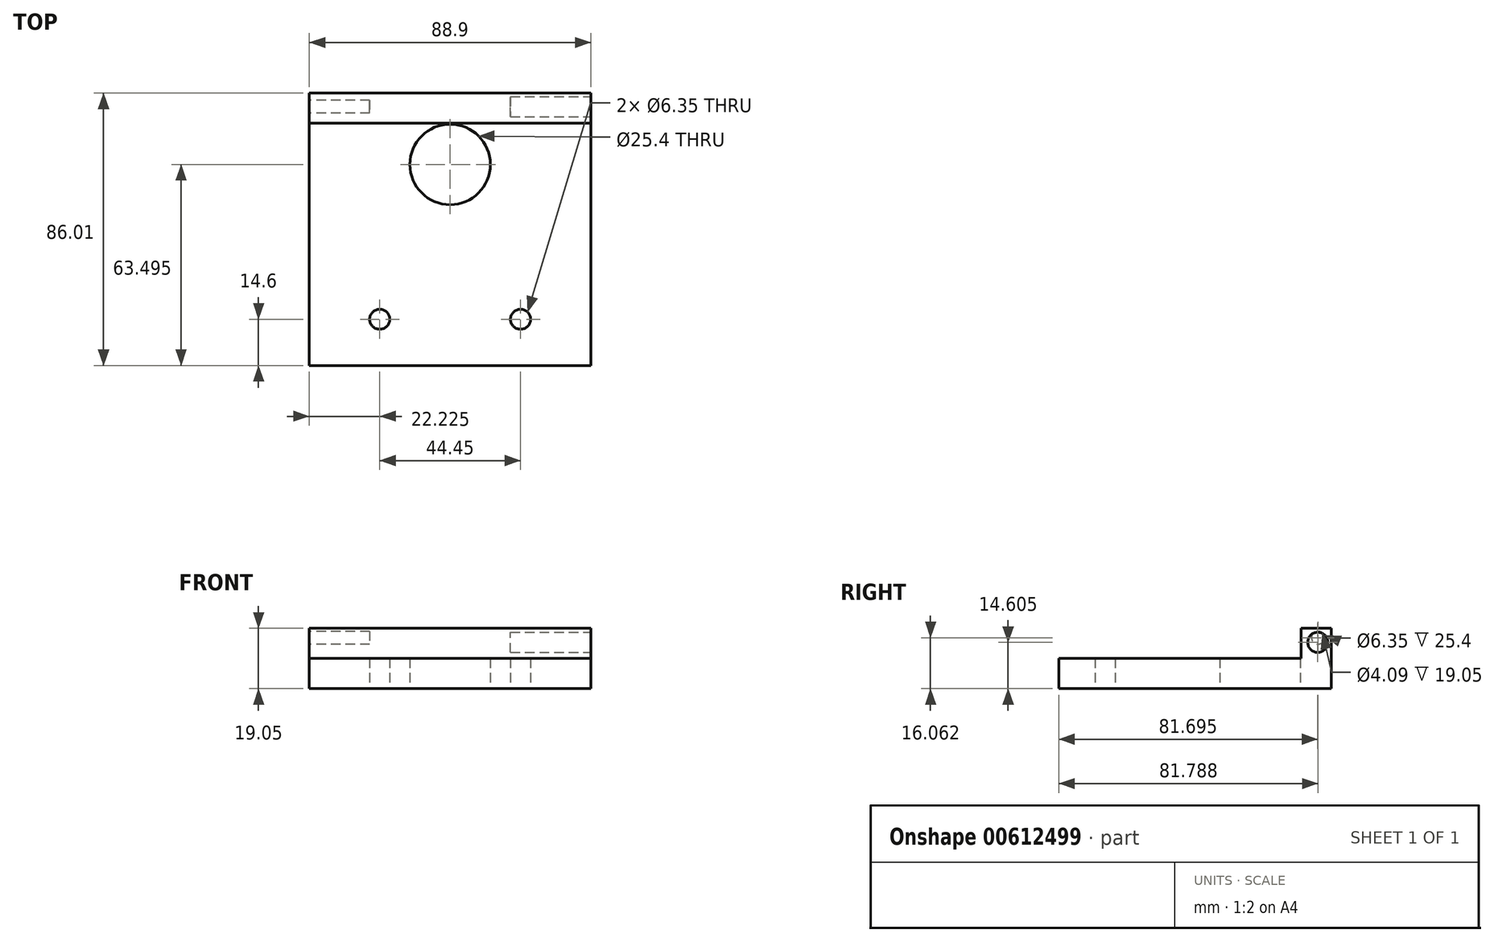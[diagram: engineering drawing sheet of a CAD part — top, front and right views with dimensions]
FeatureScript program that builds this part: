
annotation { "Feature Type Name" : "Feature", "Feature Type Description" : "" }
export const myFeature = defineFeature(function(context is Context, id is Id, definition is map)
    precondition{}
    {
        {
            var Q0;
            Q0=qCreatedBy(makeId("Top.planeOp"),FACE);
            var sketch = newSketch(context, id + "F0", { "sketchPlane" : qUnion([Q0])});
            skLineSegment(sketch, "E0.bottom", {"start": v(44.45, 41.28) * mm, "end": v(-44.45, 41.28) * mm});
            skLineSegment(sketch, "E0.top", {"start": v(44.45, -41.28) * mm, "end": v(-44.45, -41.28) * mm});
            skLineSegment(sketch, "E0.left", {"start": v(44.45, 41.28) * mm, "end": v(44.45, -41.28) * mm});
            skLineSegment(sketch, "E0.right", {"start": v(-44.45, 41.28) * mm, "end": v(-44.45, -41.28) * mm});
            skPoint(sketch, "E0.middle", {"position": v(0, 0) * mm});
            skCircle(sketch, "E1", {"center": v(0, 22.23) * mm, "radius": 12.7 * mm});
            skSolve(sketch);
        }
        {
            var Q0;
            Q0=qCreatedBy(makeId("Right.planeOp"),FACE);
            var sketch = newSketch(context, id + "F1", { "sketchPlane" : qUnion([Q0])});
            skLineSegment(sketch, "E2.bottom", {"start": v(44.74, 0) * mm, "end": v(35.22, 0) * mm});
            skLineSegment(sketch, "E2.top", {"start": v(44.74, 19.05) * mm, "end": v(35.22, 19.05) * mm});
            skLineSegment(sketch, "E2.left", {"start": v(44.74, 0) * mm, "end": v(44.74, 19.05) * mm});
            skLineSegment(sketch, "E2.right", {"start": v(35.22, 0) * mm, "end": v(35.22, 19.05) * mm});
            skLineSegment(sketch, "E3.bottom", {"start": v(47.76, 12.65) * mm, "end": v(47.53, 12.65) * mm});
            skLineSegment(sketch, "E3.top", {"start": v(47.76, 21.54) * mm, "end": v(47.53, 21.54) * mm});
            skSolve(sketch);
        }
        {
            var Q0;
            Q0=makeQuery(id+"F0.imprint","IMPRINT",FACE,{"disambiguationData":[TD([[makeQuery(id+"F0.imprint","IMPRINT",EDGE,{"derivedFrom":sQuery(id+"F0.wireOp",EDGE,"E0.bottom")}),1.0]])]});
            extrude(context, id + "F2", {"entities" : qUnion([Q0]), "depth" : 9.52 * mm, "offsetDistance" : 25.4 * mm});
        }
        {
            var Q0;
            Q0 = qSketchRegion(id + "F1", true);
            extrude(context, id + "F3", {"entities" : qUnion([Q0]), "operationType" : NewBodyOperationType.ADD, "depth" : 88.9 * mm, "offsetDistance" : 25.4 * mm, "symmetric" : true});
        }
        {
            var Q0;
            Q0=makeQuery(id+"F3.boolean.opBoolean","MERGE",FACE,{"derivedFrom":[makeQuery(id+"F2.opExtrude","SWEPT_FACE",FACE,{"disambiguationData":[OSD([sQuery(id+"F0.wireOp",EDGE,"E0.left")])]}),makeQuery(id+"F3.opExtrude","CAP_FACE",FACE,{"disambiguationData":[OSD([sQuery(id+"F1.wireOp",EDGE,"E2.bottom"),sQuery(id+"F1.wireOp",EDGE,"E2.top"),sQuery(id+"F1.wireOp",EDGE,"E2.left"),sQuery(id+"F1.wireOp",EDGE,"E2.right")])],"isStart":false})]});
            var sketch = newSketch(context, id + "F4", { "sketchPlane" : qUnion([Q0])});
            skCircle(sketch, "E4", {"center": v(40.43, 14.6) * mm, "radius": 3.18 * mm});
            skSolve(sketch);
        }
        {
            var Q0;
            Q0=makeQuery(id+"F4.imprint","IMPRINT",FACE,{"disambiguationData":[TD([[makeQuery(id+"F4.imprint","IMPRINT",EDGE,{"derivedFrom":sQuery(id+"F4.wireOp",EDGE,"E4")}),1.0]])]});
            extrude(context, id + "F5", {"entities" : qUnion([Q0]), "operationType" : NewBodyOperationType.REMOVE, "oppositeDirection" : true, "depth" : 25.4 * mm, "offsetDistance" : 25.4 * mm});
        }
        {
            var Q0;
            Q0=makeQuery(id+"F3.boolean.opBoolean","MERGE",FACE,{"derivedFrom":[makeQuery(id+"F2.opExtrude","SWEPT_FACE",FACE,{"disambiguationData":[OSD([sQuery(id+"F0.wireOp",EDGE,"E0.right")])]}),makeQuery(id+"F3.opExtrude","CAP_FACE",FACE,{"disambiguationData":[OSD([sQuery(id+"F1.wireOp",EDGE,"E2.bottom"),sQuery(id+"F1.wireOp",EDGE,"E2.top"),sQuery(id+"F1.wireOp",EDGE,"E2.left"),sQuery(id+"F1.wireOp",EDGE,"E2.right")])],"isStart":true})]});
            var sketch = newSketch(context, id + "F6", { "sketchPlane" : qUnion([Q0])});
            skCircle(sketch, "E5", {"center": v(-40.52, 16.06) * mm, "radius": 2.04 * mm});
            skSolve(sketch);
        }
        {
            var Q0;
            Q0=makeQuery(id+"F6.imprint","IMPRINT",FACE,{"disambiguationData":[TD([[makeQuery(id+"F6.imprint","IMPRINT",EDGE,{"derivedFrom":sQuery(id+"F6.wireOp",EDGE,"E5")}),1.0]])]});
            extrude(context, id + "F7", {"entities" : qUnion([Q0]), "operationType" : NewBodyOperationType.REMOVE, "oppositeDirection" : true, "depth" : 19.05 * mm, "offsetDistance" : 25.4 * mm});
        }
        {
            var Q0;
            Q0=makeQuery(id+"F3.boolean.opBoolean","MERGE",FACE,{"derivedFrom":[makeQuery(id+"F2.opExtrude","CAP_FACE",FACE,{"disambiguationData":[OSD([sQuery(id+"F0.wireOp",EDGE,"E0.bottom"),sQuery(id+"F0.wireOp",EDGE,"E0.top"),sQuery(id+"F0.wireOp",EDGE,"E0.left"),sQuery(id+"F0.wireOp",EDGE,"E0.right"),sQuery(id+"F0.wireOp",EDGE,"E1")])],"isStart":true}),makeQuery(id+"F3.opExtrude","SWEPT_FACE",FACE,{"disambiguationData":[OSD([sQuery(id+"F1.wireOp",EDGE,"E2.bottom")])]})]});
            var sketch = newSketch(context, id + "F8", { "sketchPlane" : qUnion([Q0])});
            skCircle(sketch, "E6", {"center": v(-22.23, 26.67) * mm, "radius": 3.18 * mm});
            skCircle(sketch, "E7", {"center": v(22.23, 26.67) * mm, "radius": 3.18 * mm});
            skSolve(sketch);
        }
        {
            var Q0;
            Q0=makeQuery(id+"F8.imprint","IMPRINT",FACE,{"disambiguationData":[TD([[makeQuery(id+"F8.imprint","IMPRINT",EDGE,{"derivedFrom":sQuery(id+"F8.wireOp",EDGE,"E7")}),1.0]])]});
            var Q1;
            Q1=makeQuery(id+"F8.imprint","IMPRINT",FACE,{"disambiguationData":[TD([[makeQuery(id+"F8.imprint","IMPRINT",EDGE,{"derivedFrom":sQuery(id+"F8.wireOp",EDGE,"E6")}),1.0]])]});
            extrude(context, id + "F9", {"entities" : qUnion([Q0, Q1]), "operationType" : NewBodyOperationType.REMOVE, "endBound" : BoundingType.THROUGH_ALL, "oppositeDirection" : true, "depth" : 25.4 * mm, "offsetDistance" : 25.4 * mm});
        }
    });
